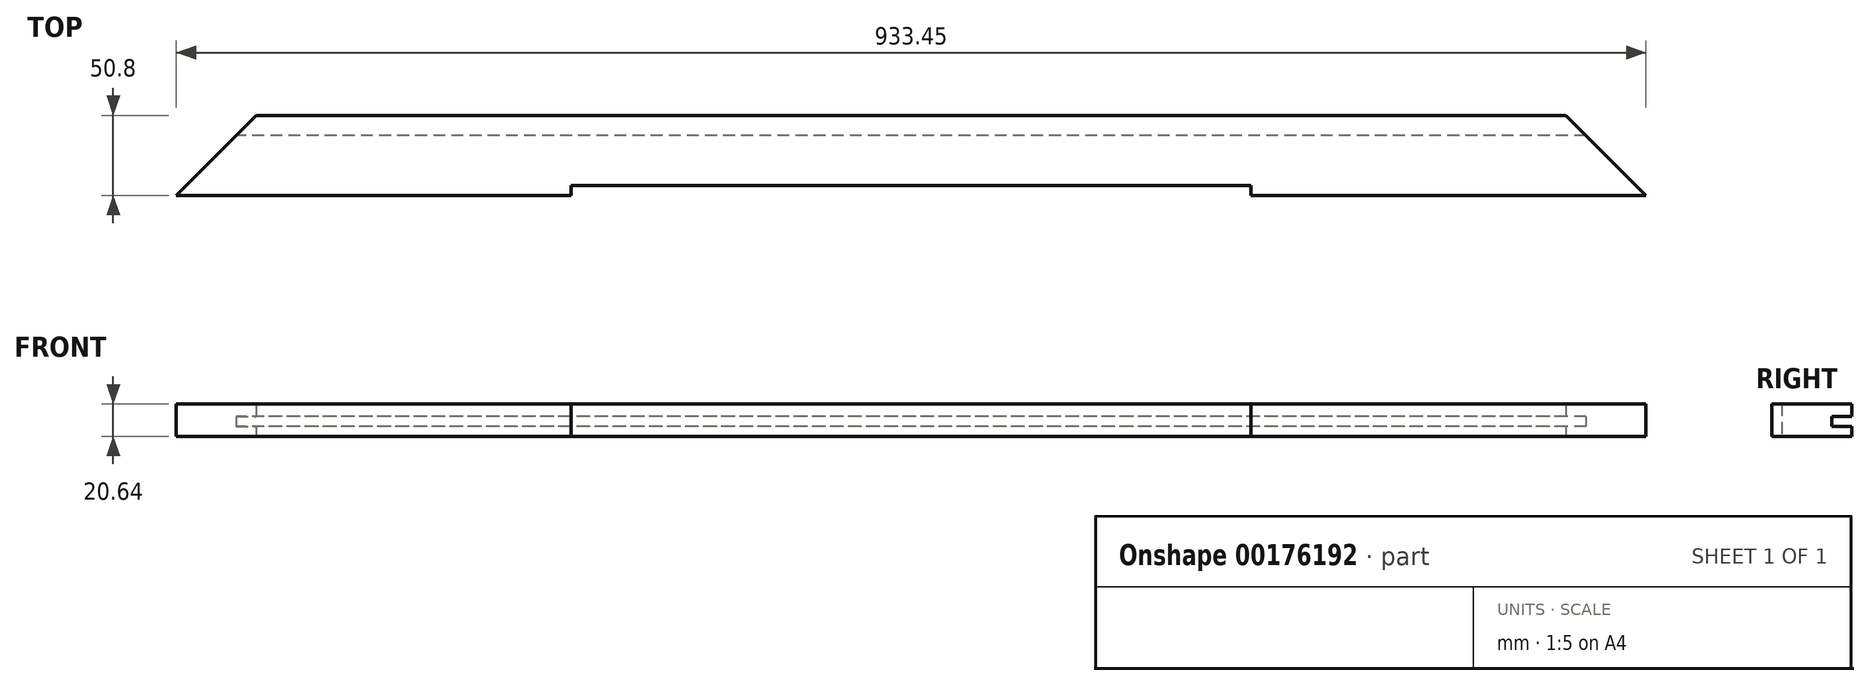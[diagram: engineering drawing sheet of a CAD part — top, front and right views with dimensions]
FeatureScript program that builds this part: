
annotation { "Feature Type Name" : "Feature", "Feature Type Description" : "" }
export const myFeature = defineFeature(function(context is Context, id is Id, definition is map)
    precondition{}
    {
        {
            var Q0;
            Q0=qCreatedBy(makeId("Top.planeOp"),FACE);
            var sketch = newSketch(context, id + "F0", { "sketchPlane" : qUnion([Q0])});
            skLineSegment(sketch, "E0.bottom", {"start": v(0, 0) * mm, "end": v(933.45, 0) * mm});
            skLineSegment(sketch, "E0.top", {"start": v(50.8, 50.8) * mm, "end": v(882.65, 50.8) * mm});
            skLineSegment(sketch, "E1", {"start": v(0, 0) * mm, "end": v(50.8, 50.8) * mm});
            skLineSegment(sketch, "E2", {"start": v(933.45, 0) * mm, "end": v(882.65, 50.8) * mm});
            skSolve(sketch);
        }
        {
            var Q0;
            Q0=makeQuery(id+"F0.imprint","IMPRINT",FACE,{"disambiguationData":[TD([[makeQuery(id+"F0.imprint","IMPRINT",EDGE,{"derivedFrom":sQuery(id+"F0.wireOp",EDGE,"E0.bottom")}),1.0]])]});
            extrude(context, id + "F1", {"entities" : qUnion([Q0]), "depth" : 20.64 * mm});
        }
        {
            var Q0;
            Q0=qCreatedBy(makeId("Right.planeOp"),FACE);
            var sketch = newSketch(context, id + "F2", { "sketchPlane" : qUnion([Q0])});
            skLineSegment(sketch, "E3.bottom", {"start": v(38.1, 12.7) * mm, "end": v(50.8, 12.7) * mm});
            skLineSegment(sketch, "E3.top", {"start": v(38.1, 6.35) * mm, "end": v(50.8, 6.35) * mm});
            skLineSegment(sketch, "E3.left", {"start": v(38.1, 12.7) * mm, "end": v(38.1, 6.35) * mm});
            skLineSegment(sketch, "E3.right", {"start": v(50.8, 12.7) * mm, "end": v(50.8, 6.35) * mm});
            skSolve(sketch);
        }
        {
            var Q0;
            Q0=makeQuery(id+"F2.imprint","IMPRINT",FACE,{"disambiguationData":[TD([[makeQuery(id+"F2.imprint","IMPRINT",EDGE,{"derivedFrom":sQuery(id+"F2.wireOp",EDGE,"E3.bottom")}),-1.0]])]});
            extrude(context, id + "F3", {"entities" : qUnion([Q0]), "operationType" : NewBodyOperationType.REMOVE, "endBound" : BoundingType.THROUGH_ALL, "depth" : 25.4 * mm});
        }
        {
            var Q0;
            Q0=makeQuery(id+"F1.opExtrude","SWEPT_FACE",FACE,{"disambiguationData":[OSD([sQuery(id+"F0.wireOp",EDGE,"E0.bottom")])]});
            var sketch = newSketch(context, id + "F4", { "sketchPlane" : qUnion([Q0])});
            skLineSegment(sketch, "E4.bottom", {"start": v(250.83, 20.64) * mm, "end": v(682.62, 20.64) * mm});
            skLineSegment(sketch, "E4.top", {"start": v(250.83, 0) * mm, "end": v(682.62, 0) * mm});
            skLineSegment(sketch, "E4.left", {"start": v(250.83, 20.64) * mm, "end": v(250.83, 0) * mm});
            skLineSegment(sketch, "E4.right", {"start": v(682.62, 20.64) * mm, "end": v(682.62, 0) * mm});
            skPoint(sketch, "E4.middle", {"position": v(466.73, 10.32) * mm});
            skPoint(sketch, "E4.middle.positionSnap0", {"position": v(466.73, 20.64) * mm});
            skPoint(sketch, "E4.centerSnap0", {"position": v(466.73, 20.64) * mm});
            skSolve(sketch);
        }
        {
            var Q0;
            Q0=makeQuery(id+"F4.imprint","IMPRINT",FACE,{"disambiguationData":[TD([[makeQuery(id+"F4.imprint","IMPRINT",EDGE,{"derivedFrom":sQuery(id+"F4.wireOp",EDGE,"E4.bottom")}),-1.0]])]});
            extrude(context, id + "F5", {"entities" : qUnion([Q0]), "operationType" : NewBodyOperationType.REMOVE, "oppositeDirection" : true, "depth" : 6.35 * mm});
        }
    });
